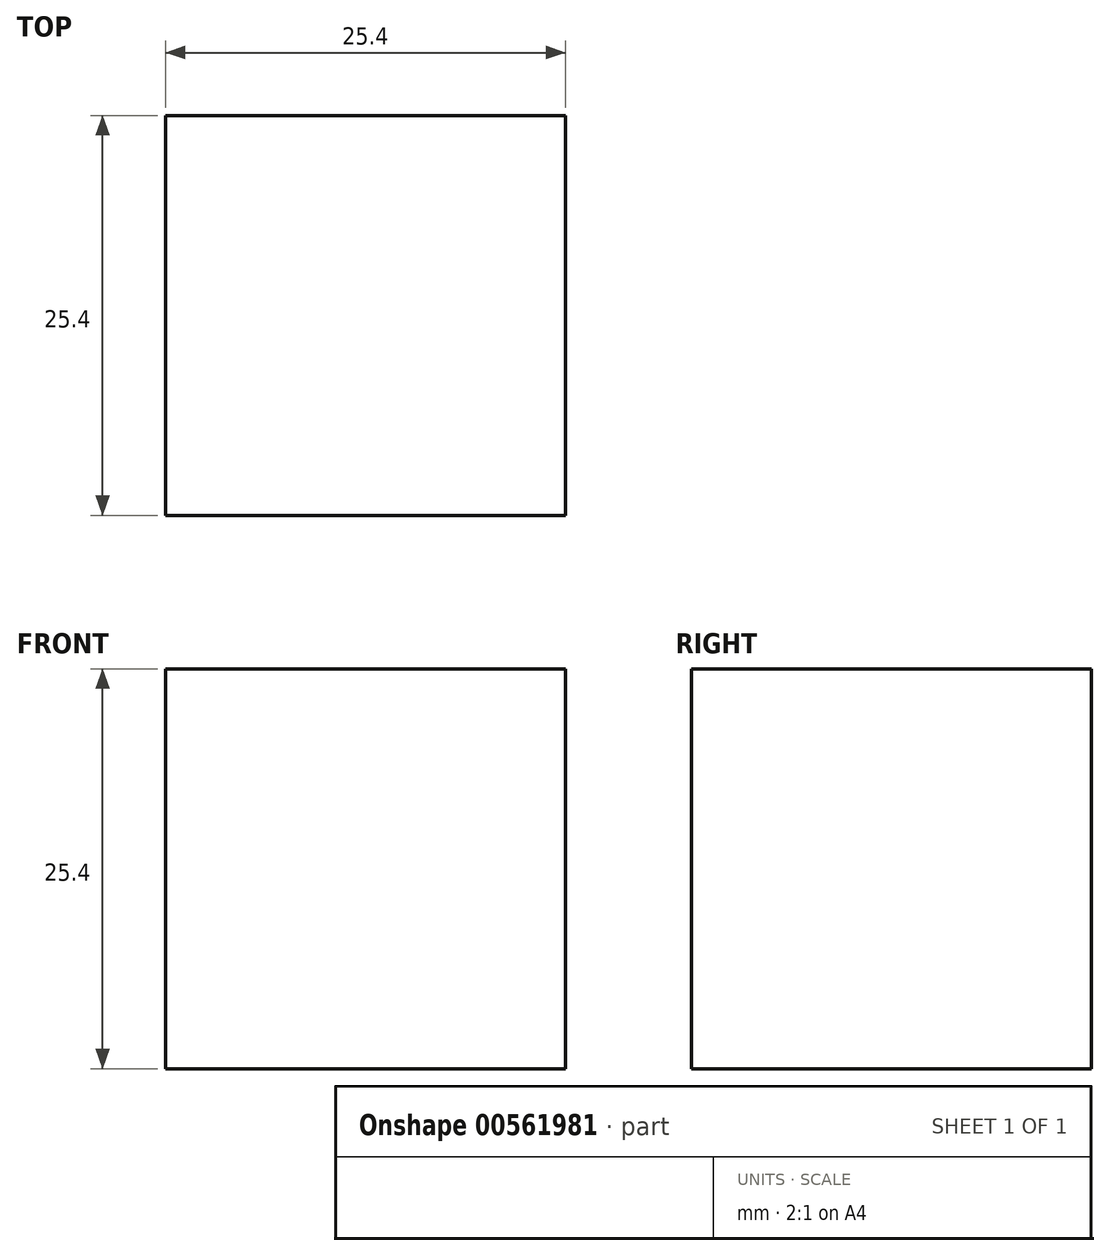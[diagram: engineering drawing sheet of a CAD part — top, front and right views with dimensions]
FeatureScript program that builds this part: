
annotation { "Feature Type Name" : "Feature", "Feature Type Description" : "" }
export const myFeature = defineFeature(function(context is Context, id is Id, definition is map)
    precondition{}
    {
        {
            var Q0;
            Q0=qCreatedBy(makeId("Front.planeOp"),FACE);
            var sketch = newSketch(context, id + "F0", { "sketchPlane" : qUnion([Q0])});
            skLineSegment(sketch, "E0.bottom", {"start": v(-25.4, 0) * mm, "end": v(0, 0) * mm});
            skLineSegment(sketch, "E0.top", {"start": v(-25.4, -25.4) * mm, "end": v(0, -25.4) * mm});
            skLineSegment(sketch, "E0.left", {"start": v(-25.4, 0) * mm, "end": v(-25.4, -25.4) * mm});
            skLineSegment(sketch, "E0.right", {"start": v(0, 0) * mm, "end": v(0, -25.4) * mm});
            skSolve(sketch);
        }
        {
            var Q0;
            Q0=makeQuery(id+"F0.imprint","IMPRINT",FACE,{"disambiguationData":[TD([[makeQuery(id+"F0.imprint","IMPRINT",EDGE,{"derivedFrom":sQuery(id+"F0.wireOp",EDGE,"E0.bottom")}),-1.0]])]});
            extrude(context, id + "F1", {"entities" : qUnion([Q0]), "depth" : 25.4 * mm, "offsetDistance" : 25.4 * mm});
        }
    });
